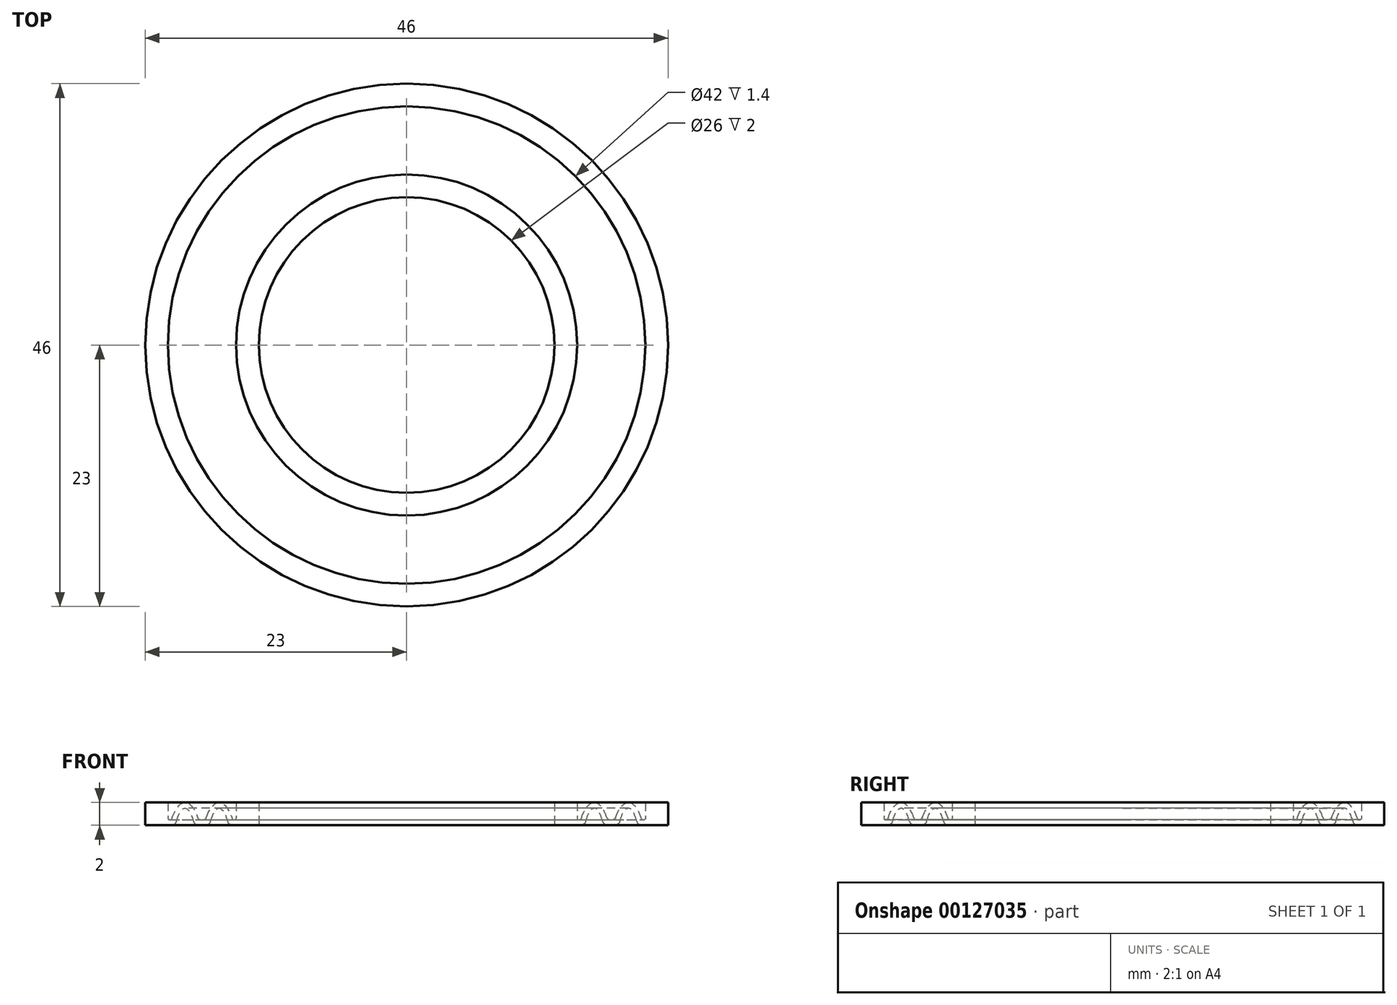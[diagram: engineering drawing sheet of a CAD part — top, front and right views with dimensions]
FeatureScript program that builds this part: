
annotation { "Feature Type Name" : "Feature", "Feature Type Description" : "" }
export const myFeature = defineFeature(function(context is Context, id is Id, definition is map)
    precondition{}
    {
        {
            var Q0;
            Q0=qCreatedBy(makeId("Front.planeOp"),FACE);
            var sketch = newSketch(context, id + "F0", { "sketchPlane" : qUnion([Q0])});
            skLineSegment(sketch, "E0.bottom", {"start": v(13, 2) * mm, "end": v(15, 2) * mm});
            skLineSegment(sketch, "E0.top", {"start": v(13, 0) * mm, "end": v(15, 0) * mm});
            skLineSegment(sketch, "E0.left", {"start": v(13, 2) * mm, "end": v(13, 0) * mm});
            skLineSegment(sketch, "E0.right", {"start": v(15, 2) * mm, "end": v(15, 0) * mm});
            skLineSegment(sketch, "E1.bottom", {"start": v(21, 2) * mm, "end": v(23, 2) * mm});
            skLineSegment(sketch, "E1.top", {"start": v(21, 0) * mm, "end": v(23, 0) * mm});
            skLineSegment(sketch, "E1.left", {"start": v(21, 2) * mm, "end": v(21, 0) * mm});
            skLineSegment(sketch, "E1.right", {"start": v(23, 2) * mm, "end": v(23, 0) * mm});
            skLineSegment(sketch, "E2", {"start": v(0, 0) * mm, "end": v(0, 2) * mm, "construction": true});
            skLineSegment(sketch, "E3", {"start": v(0, 2) * mm, "end": v(37, 2) * mm, "construction": true});
            skLineSegment(sketch, "E4", {"start": v(0, 2) * mm, "end": v(0, 4) * mm, "construction": true});
            skLineSegment(sketch, "E5", {"start": v(0, 4) * mm, "end": v(36.16, 4) * mm, "construction": true});
            skLineSegment(sketch, "E6", {"start": v(0, 0) * mm, "end": v(0, -5.25) * mm, "construction": true});
            skLineSegment(sketch, "E7", {"start": v(0, -2) * mm, "end": v(37.35, -2) * mm, "construction": true});
            skEllipse(sketch, "E8", {"center": v(16.5, -2) * mm, "majorRadius": 4 * mm, "minorRadius": 1.5 * mm, "majorAxis": v(0, 1)});
            skEllipse(sketch, "E9", {"center": v(19.5, -2) * mm, "majorRadius": 4 * mm, "minorRadius": 1.5 * mm, "majorAxis": v(0, 1)});
            skEllipse(sketch, "E10", {"center": v(16.5, -2) * mm, "majorRadius": 3.5 * mm, "minorRadius": 1 * mm, "majorAxis": v(0, 1)});
            skEllipse(sketch, "E11", {"center": v(19.5, -2) * mm, "majorRadius": 3.5 * mm, "minorRadius": 1 * mm, "majorAxis": v(0, 1)});
            skLineSegment(sketch, "E12", {"start": v(0, 0) * mm, "end": v(43.7, 0) * mm, "construction": true});
            skLineSegment(sketch, "E13", {"start": v(15, 0) * mm, "end": v(21, 0) * mm});
            skLineSegment(sketch, "E14", {"start": v(15, 0.5) * mm, "end": v(21, 0.5) * mm});
            skSolve(sketch);
        }
        {
            var Q0;
            {var subQ1=sQuery(id+"F0.wireOp",EDGE,"E0.bottom");Q0=makeQuery(id+"F0.imprint","IMPRINT",FACE,{"disambiguationData":[TD([[makeQuery(id+"F0.imprint","IMPRINT",EDGE,{"derivedFrom":subQ1}),-1.0]])]});}
            var Q1;
            {var subQ0=sQuery(id+"F0.wireOp",EDGE,"E13");var subQ5=sQuery(id+"F0.wireOp",EDGE,"E8");var subQ7=makeQuery(id+"F0.imprint","INTERSECT",VERTEX,{"disambiguationData":[OD(0.0)],"derivedFrom":[subQ5,subQ0]});Q1=makeQuery(id+"F0.imprint","IMPRINT",FACE,{"disambiguationData":[TD([[makeQuery(id+"F0.imprint","IMPRINT",EDGE,{"disambiguationData":[TD([[subQ7,1.0]])],"derivedFrom":subQ5}),-1.0]])]});}
            var Q2;
            {var subQ0=sQuery(id+"F0.wireOp",EDGE,"E13");var subQ1=sQuery(id+"F0.wireOp",EDGE,"E8");var subQ2=makeQuery(id+"F0.imprint","INTERSECT",VERTEX,{"disambiguationData":[OD(0.0)],"derivedFrom":[subQ1,subQ0]});Q2=makeQuery(id+"F0.imprint","IMPRINT",FACE,{"disambiguationData":[TD([[makeQuery(id+"F0.imprint","IMPRINT",EDGE,{"disambiguationData":[TD([[subQ2,1.0]])],"derivedFrom":subQ1}),1.0]])]});}
            var Q3;
            {var subQ0=sQuery(id+"F0.wireOp",EDGE,"E14");var subQ1=sQuery(id+"F0.wireOp",EDGE,"E8");var subQ2=makeQuery(id+"F0.imprint","INTERSECT",VERTEX,{"disambiguationData":[OD(0.0)],"derivedFrom":[subQ1,subQ0]});Q3=makeQuery(id+"F0.imprint","IMPRINT",FACE,{"disambiguationData":[TD([[makeQuery(id+"F0.imprint","IMPRINT",EDGE,{"disambiguationData":[TD([[subQ2,1.0]])],"derivedFrom":subQ1}),1.0]])]});}
            var Q4;
            {var subQ0=sQuery(id+"F0.wireOp",EDGE,"E14");var subQ1=sQuery(id+"F0.wireOp",EDGE,"E8");var subQ2=makeQuery(id+"F0.imprint","INTERSECT",VERTEX,{"disambiguationData":[OD(1.0)],"derivedFrom":[subQ1,subQ0]});Q4=makeQuery(id+"F0.imprint","IMPRINT",FACE,{"disambiguationData":[TD([[makeQuery(id+"F0.imprint","IMPRINT",EDGE,{"disambiguationData":[TD([[subQ2,1.0]])],"derivedFrom":subQ1}),1.0]])]});}
            var Q5;
            {var subQ0=sQuery(id+"F0.wireOp",EDGE,"E14");var subQ1=sQuery(id+"F0.wireOp",EDGE,"E8");var subQ2=makeQuery(id+"F0.imprint","INTERSECT",VERTEX,{"disambiguationData":[OD(1.0)],"derivedFrom":[subQ1,subQ0]});Q5=makeQuery(id+"F0.imprint","IMPRINT",FACE,{"disambiguationData":[TD([[makeQuery(id+"F0.imprint","IMPRINT",EDGE,{"disambiguationData":[TD([[subQ2,1.0]])],"derivedFrom":subQ1}),-1.0]])]});}
            var Q6;
            {var subQ0=sQuery(id+"F0.wireOp",EDGE,"E14");var subQ1=sQuery(id+"F0.wireOp",EDGE,"E9");var subQ2=makeQuery(id+"F0.imprint","INTERSECT",VERTEX,{"disambiguationData":[OD(0.0)],"derivedFrom":[subQ1,subQ0]});Q6=makeQuery(id+"F0.imprint","IMPRINT",FACE,{"disambiguationData":[TD([[makeQuery(id+"F0.imprint","IMPRINT",EDGE,{"disambiguationData":[TD([[subQ2,-1.0]])],"derivedFrom":subQ1}),1.0]])]});}
            var Q7;
            {var subQ0=sQuery(id+"F0.wireOp",EDGE,"E14");var subQ1=sQuery(id+"F0.wireOp",EDGE,"E9");var subQ2=makeQuery(id+"F0.imprint","INTERSECT",VERTEX,{"disambiguationData":[OD(0.0)],"derivedFrom":[subQ1,subQ0]});Q7=makeQuery(id+"F0.imprint","IMPRINT",FACE,{"disambiguationData":[TD([[makeQuery(id+"F0.imprint","IMPRINT",EDGE,{"disambiguationData":[TD([[subQ2,1.0]])],"derivedFrom":subQ1}),1.0]])]});}
            var Q8;
            {var subQ0=sQuery(id+"F0.wireOp",EDGE,"E13");var subQ1=sQuery(id+"F0.wireOp",EDGE,"E9");var subQ2=makeQuery(id+"F0.imprint","INTERSECT",VERTEX,{"disambiguationData":[OD(0.0)],"derivedFrom":[subQ1,subQ0]});Q8=makeQuery(id+"F0.imprint","IMPRINT",FACE,{"disambiguationData":[TD([[makeQuery(id+"F0.imprint","IMPRINT",EDGE,{"disambiguationData":[TD([[subQ2,-1.0]])],"derivedFrom":subQ1}),1.0]])]});}
            var Q9;
            {var subQ0=sQuery(id+"F0.wireOp",EDGE,"E13");var subQ5=sQuery(id+"F0.wireOp",EDGE,"E9");var subQ6=makeQuery(id+"F0.imprint","INTERSECT",VERTEX,{"disambiguationData":[OD(0.0)],"derivedFrom":[subQ5,subQ0]});Q9=makeQuery(id+"F0.imprint","IMPRINT",FACE,{"disambiguationData":[TD([[makeQuery(id+"F0.imprint","IMPRINT",EDGE,{"disambiguationData":[TD([[subQ6,-1.0]])],"derivedFrom":subQ5}),-1.0]])]});}
            var Q10;
            {var subQ3=sQuery(id+"F0.wireOp",EDGE,"E1.bottom");Q10=makeQuery(id+"F0.imprint","IMPRINT",FACE,{"disambiguationData":[TD([[makeQuery(id+"F0.imprint","IMPRINT",EDGE,{"derivedFrom":subQ3}),-1.0]])]});}
            var Q11;
            Q11=sQuery(id+"F0.wireOp",EDGE,"E2");
            revolve(context, id + "F1", {"entities" : qUnion([Q0, Q1, Q2, Q3, Q4, Q5, Q6, Q7, Q8, Q9, Q10]), "axis" : qUnion([Q11]), "revolveType" : RevolveType.FULL});
        }
        {
            var Q0;
            Q0=makeQuery(id+"F1.opRevolve","SWEPT_EDGE",EDGE,{"disambiguationData":[OSD([sQuery(id+"F0.wireOp",EDGE,"E0.right"),sQuery(id+"F0.wireOp",EDGE,"E14")])]});
            var Q1;
            {var subQ0=sQuery(id+"F0.wireOp",EDGE,"E14");var subQ1=sQuery(id+"F0.wireOp",EDGE,"E8");Q1=makeQuery(id+"F1.opRevolve","SWEPT_EDGE",EDGE,{"disambiguationData":[OSD([subQ1,subQ0]),TDD([makeQuery(id+"F0.imprint","INTERSECT",VERTEX,{"disambiguationData":[OD(0.0)],"derivedFrom":[subQ1,subQ0]})])]});}
            var Q2;
            {var subQ0=sQuery(id+"F0.wireOp",EDGE,"E14");var subQ1=sQuery(id+"F0.wireOp",EDGE,"E9");Q2=makeQuery(id+"F1.opRevolve","SWEPT_EDGE",EDGE,{"disambiguationData":[OSD([subQ1,subQ0]),TDD([makeQuery(id+"F0.imprint","INTERSECT",VERTEX,{"disambiguationData":[OD(1.0)],"derivedFrom":[subQ1,subQ0]})])]});}
            var Q3;
            Q3=makeQuery(id+"F1.opRevolve","SWEPT_EDGE",EDGE,{"disambiguationData":[OSD([sQuery(id+"F0.wireOp",EDGE,"E1.left"),sQuery(id+"F0.wireOp",EDGE,"E14")])]});
            fillet(context, id + "F2", {"entities" : qUnion([Q0, Q1, Q2, Q3]), "radius" : .1 * mm, "tangentPropagation" : true, "allowEdgeOverflow" : false});
        }
        {
            var Q0;
            {var subQ0=sQuery(id+"F0.wireOp",EDGE,"E13");var subQ1=sQuery(id+"F0.wireOp",EDGE,"E10");Q0=makeQuery(id+"F1.opRevolve","SWEPT_EDGE",EDGE,{"disambiguationData":[OSD([subQ1,subQ0]),TDD([makeQuery(id+"F0.imprint","INTERSECT",VERTEX,{"disambiguationData":[OD(0.0)],"derivedFrom":[subQ1,subQ0]})])]});}
            var Q1;
            {var subQ0=sQuery(id+"F0.wireOp",EDGE,"E13");var subQ1=sQuery(id+"F0.wireOp",EDGE,"E11");Q1=makeQuery(id+"F1.opRevolve","SWEPT_EDGE",EDGE,{"disambiguationData":[OSD([subQ1,subQ0]),TDD([makeQuery(id+"F0.imprint","INTERSECT",VERTEX,{"disambiguationData":[OD(1.0)],"derivedFrom":[subQ1,subQ0]})])]});}
            var Q2;
            {var subQ0=sQuery(id+"F0.wireOp",EDGE,"E13");var subQ1=sQuery(id+"F0.wireOp",EDGE,"E10");Q2=makeQuery(id+"F1.opRevolve","SWEPT_EDGE",EDGE,{"disambiguationData":[OSD([subQ1,subQ0]),TDD([makeQuery(id+"F0.imprint","INTERSECT",VERTEX,{"disambiguationData":[OD(1.0)],"derivedFrom":[subQ1,subQ0]})])]});}
            var Q3;
            {var subQ0=sQuery(id+"F0.wireOp",EDGE,"E13");var subQ1=sQuery(id+"F0.wireOp",EDGE,"E11");Q3=makeQuery(id+"F1.opRevolve","SWEPT_EDGE",EDGE,{"disambiguationData":[OSD([subQ1,subQ0]),TDD([makeQuery(id+"F0.imprint","INTERSECT",VERTEX,{"disambiguationData":[OD(0.0)],"derivedFrom":[subQ1,subQ0]})])]});}
            fillet(context, id + "F3", {"entities" : qUnion([Q0, Q1, Q2, Q3]), "radius" : .5 * mm, "tangentPropagation" : true, "allowEdgeOverflow" : false});
        }
        {
            var Q0;
            {var subQ0=sQuery(id+"F0.wireOp",EDGE,"E14");var subQ1=sQuery(id+"F0.wireOp",EDGE,"E9");Q0=makeQuery(id+"F1.opRevolve","SWEPT_EDGE",EDGE,{"disambiguationData":[OSD([subQ1,subQ0]),TDD([makeQuery(id+"F0.imprint","INTERSECT",VERTEX,{"disambiguationData":[OD(0.0)],"derivedFrom":[subQ1,subQ0]})])]});}
            var Q1;
            {var subQ0=sQuery(id+"F0.wireOp",EDGE,"E14");var subQ1=sQuery(id+"F0.wireOp",EDGE,"E8");Q1=makeQuery(id+"F1.opRevolve","SWEPT_EDGE",EDGE,{"disambiguationData":[OSD([subQ1,subQ0]),TDD([makeQuery(id+"F0.imprint","INTERSECT",VERTEX,{"disambiguationData":[OD(1.0)],"derivedFrom":[subQ1,subQ0]})])]});}
            fillet(context, id + "F4", {"entities" : qUnion([Q0, Q1]), "radius" : .25 * mm, "tangentPropagation" : true, "allowEdgeOverflow" : false});
        }
    });
